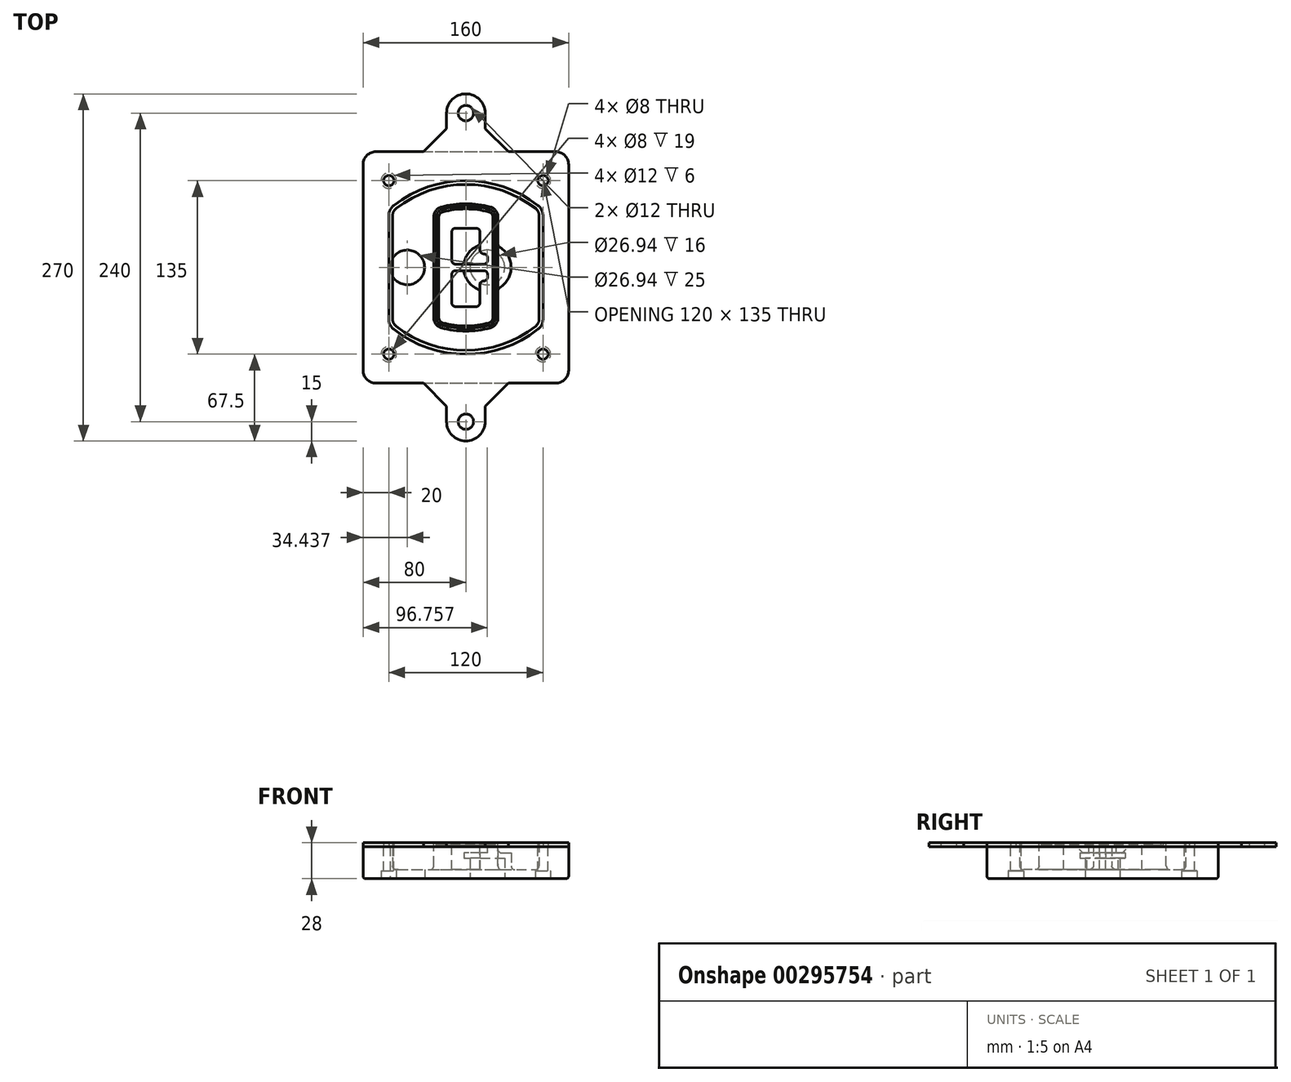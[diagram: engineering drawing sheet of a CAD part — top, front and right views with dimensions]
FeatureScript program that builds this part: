
annotation { "Feature Type Name" : "Feature", "Feature Type Description" : "" }
export const myFeature = defineFeature(function(context is Context, id is Id, definition is map)
    precondition{}
    {
        {
            var Q0;
            Q0=qCreatedBy(makeId("Top.planeOp"),FACE);
            var sketch = newSketch(context, id + "F0", { "sketchPlane" : qUnion([Q0])});
            skPoint(sketch, "E0.rect.middle", {"position": v(0, 0) * mm});
            skLineSegment(sketch, "E1.bottom", {"start": v(-70, -90) * mm, "end": v(70, -90) * mm});
            skLineSegment(sketch, "E1.top", {"start": v(-70, 90) * mm, "end": v(70, 90) * mm});
            skLineSegment(sketch, "E1.left", {"start": v(-80, -80) * mm, "end": v(-80, 80) * mm});
            skLineSegment(sketch, "E1.right", {"start": v(80, -80) * mm, "end": v(80, 80) * mm});
            skLineSegment(sketch, "E2", {"start": v(-80, 90) * mm, "end": v(80, -90) * mm, "construction": true});
            skLineSegment(sketch, "E3", {"start": v(80, 90) * mm, "end": v(-80, -90) * mm, "construction": true});
            skCircle(sketch, "E4", {"center": v(-60, 67.5) * mm, "radius": 4 * mm});
            skCircle(sketch, "E5", {"center": v(60, 67.5) * mm, "radius": 4 * mm});
            skCircle(sketch, "E6", {"center": v(60, -67.5) * mm, "radius": 4 * mm});
            skCircle(sketch, "E7", {"center": v(-60, -67.5) * mm, "radius": 4 * mm});
            skLineSegment(sketch, "E8", {"start": v(-60, 67.5) * mm, "end": v(60, 67.5) * mm, "construction": true});
            skLineSegment(sketch, "E9", {"start": v(60, 67.5) * mm, "end": v(60, -67.5) * mm, "construction": true});
            skLineSegment(sketch, "E10", {"start": v(60, -67.5) * mm, "end": v(-60, -67.5) * mm, "construction": true});
            skLineSegment(sketch, "E11", {"start": v(-60, -67.5) * mm, "end": v(-60, 67.5) * mm, "construction": true});
            skLineSegment(sketch, "E12", {"start": v(-60, 40.3) * mm, "end": v(-60, -40.3) * mm});
            skLineSegment(sketch, "E13", {"start": v(60, 40.3) * mm, "end": v(60, -40.3) * mm});
            skArc(sketch, "E14", {"start": v(56.15, 48.18) * mm, "mid": v(0, 67.5) * mm, "end": v(-56.15, 48.18) * mm});
            skArc(sketch, "E15", {"start": v(-56.15, -48.18) * mm, "mid": v(0, -67.5) * mm, "end": v(56.15, -48.18) * mm});
            skLineSegment(sketch, "E16", {"start": v(-60, 0) * mm, "end": v(60, 0) * mm, "construction": true});
            skPoint(sketch, "E17.visualSharp", {"position": v(-60, -45) * mm});
            skArc(sketch, "E17.filletArc", {"start": v(-60, -40.3) * mm, "mid": v(-58.99, -44.68) * mm, "end": v(-56.15, -48.18) * mm});
            skPoint(sketch, "E18.visualSharp", {"position": v(-60, 45) * mm});
            skArc(sketch, "E18.filletArc", {"start": v(-56.15, 48.18) * mm, "mid": v(-58.99, 44.68) * mm, "end": v(-60, 40.3) * mm});
            skPoint(sketch, "E19.visualSharp", {"position": v(60, 45) * mm});
            skArc(sketch, "E19.filletArc", {"start": v(60, 40.3) * mm, "mid": v(58.99, 44.68) * mm, "end": v(56.15, 48.18) * mm});
            skPoint(sketch, "E20.visualSharp", {"position": v(60, -45) * mm});
            skArc(sketch, "E20.filletArc", {"start": v(56.15, -48.18) * mm, "mid": v(58.99, -44.68) * mm, "end": v(60, -40.3) * mm});
            skPoint(sketch, "E21.visualSharp", {"position": v(-80, 90) * mm});
            skArc(sketch, "E21.filletArc", {"start": v(-70, 90) * mm, "mid": v(-77.07, 87.07) * mm, "end": v(-80, 80) * mm});
            skPoint(sketch, "E22.visualSharp", {"position": v(80, 90) * mm});
            skArc(sketch, "E22.filletArc", {"start": v(80, 80) * mm, "mid": v(77.07, 87.07) * mm, "end": v(70, 90) * mm});
            skPoint(sketch, "E23.visualSharp", {"position": v(80, -90) * mm});
            skArc(sketch, "E23.filletArc", {"start": v(70, -90) * mm, "mid": v(77.07, -87.07) * mm, "end": v(80, -80) * mm});
            skPoint(sketch, "E24.visualSharp", {"position": v(-80, -90) * mm});
            skArc(sketch, "E24.filletArc", {"start": v(-80, -80) * mm, "mid": v(-77.07, -87.07) * mm, "end": v(-70, -90) * mm});
            skArc(sketch, "E25.0", {"start": v(57, 40.3) * mm, "mid": v(56.3, 43.36) * mm, "end": v(54.3, 45.81) * mm});
            skLineSegment(sketch, "E25.1", {"start": v(57, 40.3) * mm, "end": v(57, -40.3) * mm});
            skArc(sketch, "E25.2", {"start": v(54.3, -45.81) * mm, "mid": v(56.3, -43.36) * mm, "end": v(57, -40.3) * mm});
            skArc(sketch, "E25.3", {"start": v(-54.3, -45.81) * mm, "mid": v(0, -64.5) * mm, "end": v(54.3, -45.81) * mm});
            skArc(sketch, "E25.4", {"start": v(-57, -40.3) * mm, "mid": v(-56.3, -43.36) * mm, "end": v(-54.3, -45.81) * mm});
            skArc(sketch, "E25.5", {"start": v(54.3, 45.81) * mm, "mid": v(0, 64.5) * mm, "end": v(-54.3, 45.81) * mm});
            skLineSegment(sketch, "E25.6", {"start": v(-57, 40.3) * mm, "end": v(-57, -40.3) * mm});
            skArc(sketch, "E25.7", {"start": v(-54.3, 45.81) * mm, "mid": v(-56.3, 43.36) * mm, "end": v(-57, 40.3) * mm});
            skArc(sketch, "E26.0", {"start": v(-58.62, 51.33) * mm, "mid": v(-62.58, 46.43) * mm, "end": v(-64, 40.3) * mm});
            skArc(sketch, "E26.1", {"start": v(58.62, 51.33) * mm, "mid": v(0, 71.5) * mm, "end": v(-58.62, 51.33) * mm});
            skArc(sketch, "E26.2", {"start": v(64, 40.3) * mm, "mid": v(62.58, 46.43) * mm, "end": v(58.62, 51.33) * mm});
            skLineSegment(sketch, "E26.3", {"start": v(64, 40.3) * mm, "end": v(64, -40.3) * mm});
            skArc(sketch, "E26.4", {"start": v(58.62, -51.33) * mm, "mid": v(62.58, -46.43) * mm, "end": v(64, -40.3) * mm});
            skLineSegment(sketch, "E26.5", {"start": v(-64, 40.3) * mm, "end": v(-64, -40.3) * mm});
            skArc(sketch, "E26.6", {"start": v(-58.62, -51.33) * mm, "mid": v(0, -71.5) * mm, "end": v(58.62, -51.33) * mm});
            skArc(sketch, "E26.7", {"start": v(-64, -40.3) * mm, "mid": v(-62.58, -46.43) * mm, "end": v(-58.62, -51.33) * mm});
            skSolve(sketch);
        }
        {
            var Q0;
            Q0=makeQuery(id+"F0.imprint","IMPRINT",FACE,{"disambiguationData":[TD([[makeQuery(id+"F0.imprint","IMPRINT",EDGE,{"derivedFrom":sQuery(id+"F0.wireOp",EDGE,"E1.bottom")}),1.0]])]});
            var Q1;
            Q1=makeQuery(id+"F0.imprint","IMPRINT",FACE,{"disambiguationData":[TD([[makeQuery(id+"F0.imprint","IMPRINT",EDGE,{"derivedFrom":sQuery(id+"F0.wireOp",EDGE,"E12")}),1.0]])]});
            var Q2;
            Q2=makeQuery(id+"F0.imprint","IMPRINT",FACE,{"disambiguationData":[TD([[makeQuery(id+"F0.imprint","IMPRINT",EDGE,{"derivedFrom":sQuery(id+"F0.wireOp",EDGE,"E25.0")}),1.0]])]});
            var Q3;
            Q3=makeQuery(id+"F0.imprint","IMPRINT",FACE,{"disambiguationData":[TD([[makeQuery(id+"F0.imprint","IMPRINT",EDGE,{"derivedFrom":sQuery(id+"F0.wireOp",EDGE,"E12")}),-1.0]])]});
            extrude(context, id + "F1", {"entities" : qUnion([Q0, Q1, Q2, Q3]), "oppositeDirection" : true, "depth" : 25 * mm});
        }
        {
            var Q0;
            Q0=makeQuery(id+"F0.imprint","IMPRINT",FACE,{"disambiguationData":[TD([[makeQuery(id+"F0.imprint","IMPRINT",EDGE,{"derivedFrom":sQuery(id+"F0.wireOp",EDGE,"E12")}),1.0]])]});
            extrude(context, id + "F2", {"entities" : qUnion([Q0]), "operationType" : NewBodyOperationType.ADD, "depth" : 3 * mm});
        }
        {
            var Q0;
            Q0=makeQuery(id+"F0.imprint","IMPRINT",FACE,{"disambiguationData":[TD([[makeQuery(id+"F0.imprint","IMPRINT",EDGE,{"derivedFrom":sQuery(id+"F0.wireOp",EDGE,"E25.0")}),1.0]])]});
            extrude(context, id + "F3", {"entities" : qUnion([Q0]), "operationType" : NewBodyOperationType.REMOVE, "oppositeDirection" : true, "depth" : 18 * mm});
        }
        {
            var Q0;
            Q0=makeQuery(id+"F2.opExtrude","CAP_FACE",FACE,{"disambiguationData":[OSD([sQuery(id+"F0.wireOp",EDGE,"E12"),sQuery(id+"F0.wireOp",EDGE,"E13"),sQuery(id+"F0.wireOp",EDGE,"E14"),sQuery(id+"F0.wireOp",EDGE,"E15"),sQuery(id+"F0.wireOp",EDGE,"E17.filletArc"),sQuery(id+"F0.wireOp",EDGE,"E18.filletArc"),sQuery(id+"F0.wireOp",EDGE,"E19.filletArc"),sQuery(id+"F0.wireOp",EDGE,"E20.filletArc"),sQuery(id+"F0.wireOp",EDGE,"E25.0"),sQuery(id+"F0.wireOp",EDGE,"E25.1"),sQuery(id+"F0.wireOp",EDGE,"E25.2"),sQuery(id+"F0.wireOp",EDGE,"E25.3"),sQuery(id+"F0.wireOp",EDGE,"E25.4"),sQuery(id+"F0.wireOp",EDGE,"E25.5"),sQuery(id+"F0.wireOp",EDGE,"E25.6"),sQuery(id+"F0.wireOp",EDGE,"E25.7")])],"isStart":false});
            var sketch = newSketch(context, id + "F4", { "sketchPlane" : qUnion([Q0])});
            skArc(sketch, "E27.0", {"start": v(-19.08, -46.97) * mm, "mid": v(0, -49.5) * mm, "end": v(19.08, -46.97) * mm});
            skArc(sketch, "E28.0", {"start": v(19.08, 46.97) * mm, "mid": v(0, 49.5) * mm, "end": v(-19.08, 46.97) * mm});
            skLineSegment(sketch, "E29", {"start": v(-25, 39.25) * mm, "end": v(-25, -39.25) * mm});
            skLineSegment(sketch, "E30", {"start": v(25, 39.25) * mm, "end": v(25, -39.25) * mm});
            skLineSegment(sketch, "E31", {"start": v(-25, 45.1) * mm, "end": v(25, 45.1) * mm, "construction": true});
            skLineSegment(sketch, "E32", {"start": v(-25, -45.1) * mm, "end": v(25, -45.1) * mm, "construction": true});
            skPoint(sketch, "E33.visualSharp", {"position": v(-25, 45.1) * mm});
            skArc(sketch, "E33.filletArc", {"start": v(-19.08, 46.97) * mm, "mid": v(-23.35, 44.11) * mm, "end": v(-25, 39.25) * mm});
            skPoint(sketch, "E34.visualSharp", {"position": v(25, 45.1) * mm});
            skArc(sketch, "E34.filletArc", {"start": v(25, 39.25) * mm, "mid": v(23.35, 44.11) * mm, "end": v(19.08, 46.97) * mm});
            skPoint(sketch, "E35.visualSharp", {"position": v(25, -45.1) * mm});
            skArc(sketch, "E35.filletArc", {"start": v(19.08, -46.97) * mm, "mid": v(23.35, -44.11) * mm, "end": v(25, -39.25) * mm});
            skPoint(sketch, "E36.visualSharp", {"position": v(-25, -45.1) * mm});
            skArc(sketch, "E36.filletArc", {"start": v(-25, -39.25) * mm, "mid": v(-23.35, -44.11) * mm, "end": v(-19.08, -46.97) * mm});
            skArc(sketch, "E37.0", {"start": v(54.3, 45.81) * mm, "mid": v(0, 64.5) * mm, "end": v(-54.3, 45.81) * mm});
            skArc(sketch, "E37.1", {"start": v(-54.3, 45.81) * mm, "mid": v(-56.3, 43.36) * mm, "end": v(-57, 40.3) * mm});
            skLineSegment(sketch, "E37.2", {"start": v(-57, 40.3) * mm, "end": v(-57, -40.3) * mm});
            skArc(sketch, "E37.3", {"start": v(-57, -40.3) * mm, "mid": v(-56.3, -43.36) * mm, "end": v(-54.3, -45.81) * mm});
            skArc(sketch, "E37.4", {"start": v(-54.3, -45.81) * mm, "mid": v(0, -64.5) * mm, "end": v(54.3, -45.81) * mm});
            skArc(sketch, "E37.5", {"start": v(54.3, -45.81) * mm, "mid": v(56.3, -43.36) * mm, "end": v(57, -40.3) * mm});
            skLineSegment(sketch, "E37.6", {"start": v(57, 40.3) * mm, "end": v(57, -40.3) * mm});
            skArc(sketch, "E37.7", {"start": v(57, 40.3) * mm, "mid": v(56.3, 43.36) * mm, "end": v(54.3, 45.81) * mm});
            skLineSegment(sketch, "E38.0", {"start": v(23, 39.25) * mm, "end": v(23, -39.25) * mm});
            skArc(sketch, "E38.1", {"start": v(18.56, -45.04) * mm, "mid": v(21.76, -42.9) * mm, "end": v(23, -39.25) * mm});
            skArc(sketch, "E38.2", {"start": v(-18.56, -45.04) * mm, "mid": v(0, -47.5) * mm, "end": v(18.56, -45.04) * mm});
            skArc(sketch, "E38.3", {"start": v(-23, -39.25) * mm, "mid": v(-21.76, -42.9) * mm, "end": v(-18.56, -45.04) * mm});
            skLineSegment(sketch, "E38.4", {"start": v(-23, 39.25) * mm, "end": v(-23, -39.25) * mm});
            skArc(sketch, "E38.5", {"start": v(23, 39.25) * mm, "mid": v(21.76, 42.9) * mm, "end": v(18.56, 45.04) * mm});
            skArc(sketch, "E38.6", {"start": v(-18.56, 45.04) * mm, "mid": v(-21.76, 42.9) * mm, "end": v(-23, 39.25) * mm});
            skArc(sketch, "E38.7", {"start": v(18.56, 45.04) * mm, "mid": v(0, 47.5) * mm, "end": v(-18.56, 45.04) * mm});
            skArc(sketch, "E39.0", {"start": v(21, 39.25) * mm, "mid": v(20.18, 41.68) * mm, "end": v(18.04, 43.1) * mm});
            skLineSegment(sketch, "E39.1", {"start": v(21, 39.25) * mm, "end": v(21, -39.25) * mm});
            skArc(sketch, "E39.2", {"start": v(18.04, -43.1) * mm, "mid": v(20.18, -41.68) * mm, "end": v(21, -39.25) * mm});
            skArc(sketch, "E39.3", {"start": v(-18.04, -43.1) * mm, "mid": v(0, -45.5) * mm, "end": v(18.04, -43.1) * mm});
            skArc(sketch, "E39.4", {"start": v(-21, -39.25) * mm, "mid": v(-20.18, -41.68) * mm, "end": v(-18.04, -43.1) * mm});
            skArc(sketch, "E39.5", {"start": v(18.04, 43.1) * mm, "mid": v(0, 45.5) * mm, "end": v(-18.04, 43.1) * mm});
            skLineSegment(sketch, "E39.6", {"start": v(-21, 39.25) * mm, "end": v(-21, -39.25) * mm});
            skArc(sketch, "E39.7", {"start": v(-18.04, 43.1) * mm, "mid": v(-20.18, 41.68) * mm, "end": v(-21, 39.25) * mm});
            skLineSegment(sketch, "E40", {"start": v(-25, 0) * mm, "end": v(25, 0) * mm, "construction": true});
            skLineSegment(sketch, "E41", {"start": v(-11, 5.5) * mm, "end": v(-11, 27.5) * mm});
            skLineSegment(sketch, "E42", {"start": v(-8, 30.5) * mm, "end": v(8, 30.5) * mm});
            skLineSegment(sketch, "E43", {"start": v(11, 27.5) * mm, "end": v(11, 13.5) * mm});
            skLineSegment(sketch, "E44", {"start": v(14, 10.5) * mm, "end": v(14, 10.5) * mm});
            skLineSegment(sketch, "E45", {"start": v(17, 7.5) * mm, "end": v(17, 5.5) * mm});
            skLineSegment(sketch, "E46", {"start": v(14, 2.5) * mm, "end": v(-8, 2.5) * mm});
            skPoint(sketch, "E47.visualSharp", {"position": v(-11, 30.5) * mm});
            skArc(sketch, "E47.filletArc", {"start": v(-8, 30.5) * mm, "mid": v(-10.12, 29.62) * mm, "end": v(-11, 27.5) * mm});
            skPoint(sketch, "E48.visualSharp", {"position": v(11, 30.5) * mm});
            skArc(sketch, "E48.filletArc", {"start": v(11, 27.5) * mm, "mid": v(10.12, 29.62) * mm, "end": v(8, 30.5) * mm});
            skPoint(sketch, "E49.visualSharp", {"position": v(11, 10.5) * mm});
            skArc(sketch, "E49.filletArc", {"start": v(11, 13.5) * mm, "mid": v(11.88, 11.38) * mm, "end": v(14, 10.5) * mm});
            skPoint(sketch, "E50.visualSharp", {"position": v(17, 10.5) * mm});
            skArc(sketch, "E50.filletArc", {"start": v(17, 7.5) * mm, "mid": v(16.12, 9.62) * mm, "end": v(14, 10.5) * mm});
            skPoint(sketch, "E51.visualSharp", {"position": v(17, 2.5) * mm});
            skArc(sketch, "E51.filletArc", {"start": v(14, 2.5) * mm, "mid": v(16.12, 3.38) * mm, "end": v(17, 5.5) * mm});
            skPoint(sketch, "E52.visualSharp", {"position": v(-11, 2.5) * mm});
            skArc(sketch, "E52.filletArc", {"start": v(-11, 5.5) * mm, "mid": v(-10.12, 3.38) * mm, "end": v(-8, 2.5) * mm});
            skLineSegment(sketch, "E53.0.MirrorCS", {"start": v(14, -2.5) * mm, "end": v(-8, -2.5) * mm});
            skArc(sketch, "E54.0.MirrorCS", {"start": v(-11, -5.5) * mm, "mid": v(-10.12, -3.38) * mm, "end": v(-8, -2.5) * mm});
            skLineSegment(sketch, "E55.0.MirrorCS", {"start": v(-11, -5.5) * mm, "end": v(-11, -27.5) * mm});
            skArc(sketch, "E56.0.MirrorCS", {"start": v(-8, -30.5) * mm, "mid": v(-10.12, -29.62) * mm, "end": v(-11, -27.5) * mm});
            skLineSegment(sketch, "E57.0.MirrorCS", {"start": v(-8, -30.5) * mm, "end": v(8, -30.5) * mm});
            skArc(sketch, "E58.0.MirrorCS", {"start": v(11, -27.5) * mm, "mid": v(10.12, -29.62) * mm, "end": v(8, -30.5) * mm});
            skLineSegment(sketch, "E59.0.MirrorCS", {"start": v(11, -27.5) * mm, "end": v(11, -13.5) * mm});
            skArc(sketch, "E60.0.MirrorCS", {"start": v(11, -13.5) * mm, "mid": v(11.88, -11.38) * mm, "end": v(14, -10.5) * mm});
            skArc(sketch, "E61.0.MirrorCS", {"start": v(17, -7.5) * mm, "mid": v(16.12, -9.62) * mm, "end": v(14, -10.5) * mm});
            skLineSegment(sketch, "E62.0.MirrorCS", {"start": v(17, -7.5) * mm, "end": v(17, -5.5) * mm});
            skArc(sketch, "E63.0.MirrorCS", {"start": v(14, -2.5) * mm, "mid": v(16.12, -3.38) * mm, "end": v(17, -5.5) * mm});
            skSolve(sketch);
        }
        {
            var Q0;
            Q0=makeQuery(id+"F4.imprint","IMPRINT",FACE,{"disambiguationData":[TD([[makeQuery(id+"F4.imprint","IMPRINT",EDGE,{"derivedFrom":sQuery(id+"F4.wireOp",EDGE,"E27.0")}),1.0]])]});
            var Q1;
            Q1=makeQuery(id+"F4.imprint","IMPRINT",FACE,{"disambiguationData":[TD([[makeQuery(id+"F4.imprint","IMPRINT",EDGE,{"derivedFrom":sQuery(id+"F4.wireOp",EDGE,"E38.0")}),-1.0]])]});
            var Q2;
            Q2=makeQuery(id+"F4.imprint","IMPRINT",FACE,{"disambiguationData":[TD([[makeQuery(id+"F4.imprint","IMPRINT",EDGE,{"derivedFrom":sQuery(id+"F4.wireOp",EDGE,"E39.0")}),1.0]])]});
            extrude(context, id + "F5", {"entities" : qUnion([Q0, Q1, Q2]), "operationType" : NewBodyOperationType.ADD, "endBound" : BoundingType.UP_TO_NEXT, "oppositeDirection" : true, "depth" : 25 * mm});
        }
        {
            var Q0;
            Q0=makeQuery(id+"F4.imprint","IMPRINT",FACE,{"disambiguationData":[TD([[makeQuery(id+"F4.imprint","IMPRINT",EDGE,{"derivedFrom":sQuery(id+"F4.wireOp",EDGE,"E38.0")}),-1.0]])]});
            extrude(context, id + "F6", {"entities" : qUnion([Q0]), "operationType" : NewBodyOperationType.REMOVE, "oppositeDirection" : true, "depth" : 2 * mm});
        }
        {
            var Q0;
            Q0=makeQuery(id+"F1.opExtrude","CAP_FACE",FACE,{"disambiguationData":[OSD([sQuery(id+"F0.wireOp",EDGE,"E1.bottom"),sQuery(id+"F0.wireOp",EDGE,"E1.top"),sQuery(id+"F0.wireOp",EDGE,"E1.left"),sQuery(id+"F0.wireOp",EDGE,"E1.right"),sQuery(id+"F0.wireOp",EDGE,"E4"),sQuery(id+"F0.wireOp",EDGE,"E5"),sQuery(id+"F0.wireOp",EDGE,"E6"),sQuery(id+"F0.wireOp",EDGE,"E7"),sQuery(id+"F0.wireOp",EDGE,"E21.filletArc"),sQuery(id+"F0.wireOp",EDGE,"E22.filletArc"),sQuery(id+"F0.wireOp",EDGE,"E23.filletArc"),sQuery(id+"F0.wireOp",EDGE,"E24.filletArc")])],"isStart":false});
            var sketch = newSketch(context, id + "F7", { "sketchPlane" : qUnion([Q0])});
            skCircle(sketch, "E64", {"center": v(16.76, 0) * mm, "radius": 13.47 * mm});
            skCircle(sketch, "E65", {"center": v(-45.56, 0) * mm, "radius": 13.47 * mm});
            skLineSegment(sketch, "E66", {"start": v(80, 0) * mm, "end": v(-80, 0) * mm});
            skCircle(sketch, "E67", {"center": v(16.76, 0) * mm, "radius": 18.47 * mm});
            skCircle(sketch, "E68", {"center": v(60, -67.5) * mm, "radius": 6 * mm});
            skCircle(sketch, "E69", {"center": v(-60, -67.5) * mm, "radius": 6 * mm});
            skCircle(sketch, "E70", {"center": v(-60, 67.5) * mm, "radius": 6 * mm});
            skCircle(sketch, "E71", {"center": v(60, 67.5) * mm, "radius": 6 * mm});
            skSolve(sketch);
        }
        {
            var Q0;
            {var subQ1=sQuery(id+"F7.wireOp",EDGE,"E66");var subQ4=sQuery(id+"F7.wireOp",EDGE,"E64");var subQ6=makeQuery(id+"F7.imprint","INTERSECT",VERTEX,{"disambiguationData":[OD(0.0)],"derivedFrom":[subQ4,subQ1]});Q0=makeQuery(id+"F7.imprint","IMPRINT",FACE,{"disambiguationData":[TD([[makeQuery(id+"F7.imprint","IMPRINT",EDGE,{"disambiguationData":[TD([[subQ6,-1.0]])],"derivedFrom":subQ4}),-1.0]])]});}
            var Q1;
            {var subQ0=sQuery(id+"F7.wireOp",EDGE,"E66");var subQ1=sQuery(id+"F7.wireOp",EDGE,"E64");var subQ3=makeQuery(id+"F7.imprint","INTERSECT",VERTEX,{"disambiguationData":[OD(0.0)],"derivedFrom":[subQ1,subQ0]});Q1=makeQuery(id+"F7.imprint","IMPRINT",FACE,{"disambiguationData":[TD([[makeQuery(id+"F7.imprint","IMPRINT",EDGE,{"disambiguationData":[TD([[subQ3,-1.0]])],"derivedFrom":subQ1}),1.0]])]});}
            var Q2;
            {var subQ0=sQuery(id+"F7.wireOp",EDGE,"E66");var subQ1=sQuery(id+"F7.wireOp",EDGE,"E64");var subQ3=makeQuery(id+"F7.imprint","INTERSECT",VERTEX,{"disambiguationData":[OD(0.0)],"derivedFrom":[subQ1,subQ0]});Q2=makeQuery(id+"F7.imprint","IMPRINT",FACE,{"disambiguationData":[TD([[makeQuery(id+"F7.imprint","IMPRINT",EDGE,{"disambiguationData":[TD([[subQ3,1.0]])],"derivedFrom":subQ1}),1.0]])]});}
            var Q3;
            {var subQ1=sQuery(id+"F7.wireOp",EDGE,"E66");var subQ4=sQuery(id+"F7.wireOp",EDGE,"E64");var subQ6=makeQuery(id+"F7.imprint","INTERSECT",VERTEX,{"disambiguationData":[OD(0.0)],"derivedFrom":[subQ4,subQ1]});Q3=makeQuery(id+"F7.imprint","IMPRINT",FACE,{"disambiguationData":[TD([[makeQuery(id+"F7.imprint","IMPRINT",EDGE,{"disambiguationData":[TD([[subQ6,1.0]])],"derivedFrom":subQ4}),-1.0]])]});}
            extrude(context, id + "F8", {"entities" : qUnion([Q0, Q1, Q2, Q3]), "operationType" : NewBodyOperationType.ADD, "oppositeDirection" : true, "depth" : 20 * mm});
        }
        {
            var Q0;
            {var subQ0=sQuery(id+"F7.wireOp",EDGE,"E66");var subQ1=sQuery(id+"F7.wireOp",EDGE,"E64");var subQ3=makeQuery(id+"F7.imprint","INTERSECT",VERTEX,{"disambiguationData":[OD(0.0)],"derivedFrom":[subQ1,subQ0]});Q0=makeQuery(id+"F7.imprint","IMPRINT",FACE,{"disambiguationData":[TD([[makeQuery(id+"F7.imprint","IMPRINT",EDGE,{"disambiguationData":[TD([[subQ3,-1.0]])],"derivedFrom":subQ1}),1.0]])]});}
            var Q1;
            {var subQ0=sQuery(id+"F7.wireOp",EDGE,"E66");var subQ1=sQuery(id+"F7.wireOp",EDGE,"E64");var subQ3=makeQuery(id+"F7.imprint","INTERSECT",VERTEX,{"disambiguationData":[OD(0.0)],"derivedFrom":[subQ1,subQ0]});Q1=makeQuery(id+"F7.imprint","IMPRINT",FACE,{"disambiguationData":[TD([[makeQuery(id+"F7.imprint","IMPRINT",EDGE,{"disambiguationData":[TD([[subQ3,1.0]])],"derivedFrom":subQ1}),1.0]])]});}
            extrude(context, id + "F9", {"entities" : qUnion([Q0, Q1]), "operationType" : NewBodyOperationType.REMOVE, "oppositeDirection" : true, "depth" : 16 * mm});
        }
        {
            var Q0;
            {var subQ0=sQuery(id+"F7.wireOp",EDGE,"E66");var subQ1=sQuery(id+"F7.wireOp",EDGE,"E65");var subQ3=makeQuery(id+"F7.imprint","INTERSECT",VERTEX,{"disambiguationData":[OD(0.0)],"derivedFrom":[subQ1,subQ0]});Q0=makeQuery(id+"F7.imprint","IMPRINT",FACE,{"disambiguationData":[TD([[makeQuery(id+"F7.imprint","IMPRINT",EDGE,{"disambiguationData":[TD([[subQ3,-1.0]])],"derivedFrom":subQ1}),1.0]])]});}
            var Q1;
            {var subQ0=sQuery(id+"F7.wireOp",EDGE,"E66");var subQ1=sQuery(id+"F7.wireOp",EDGE,"E65");var subQ3=makeQuery(id+"F7.imprint","INTERSECT",VERTEX,{"disambiguationData":[OD(0.0)],"derivedFrom":[subQ1,subQ0]});Q1=makeQuery(id+"F7.imprint","IMPRINT",FACE,{"disambiguationData":[TD([[makeQuery(id+"F7.imprint","IMPRINT",EDGE,{"disambiguationData":[TD([[subQ3,1.0]])],"derivedFrom":subQ1}),1.0]])]});}
            extrude(context, id + "F10", {"entities" : qUnion([Q0, Q1]), "operationType" : NewBodyOperationType.REMOVE, "oppositeDirection" : true, "depth" : 25 * mm});
        }
        {
            var Q0;
            Q0=makeQuery(id+"F7.imprint","IMPRINT",FACE,{"disambiguationData":[TD([[makeQuery(id+"F7.imprint","IMPRINT",EDGE,{"derivedFrom":sQuery(id+"F7.wireOp",EDGE,"E68")}),1.0]])]});
            var Q1;
            Q1=makeQuery(id+"F7.imprint","IMPRINT",FACE,{"disambiguationData":[TD([[makeQuery(id+"F7.imprint","IMPRINT",EDGE,{"derivedFrom":makeQuery(id+"F1.opExtrude","CAP_EDGE",EDGE,{"disambiguationData":[OSD([sQuery(id+"F0.wireOp",EDGE,"E5")])],"isStart":false})}),-1.0]])]});
            var Q2;
            Q2=makeQuery(id+"F7.imprint","IMPRINT",FACE,{"disambiguationData":[TD([[makeQuery(id+"F7.imprint","IMPRINT",EDGE,{"derivedFrom":sQuery(id+"F7.wireOp",EDGE,"E69")}),1.0]])]});
            var Q3;
            Q3=makeQuery(id+"F7.imprint","IMPRINT",FACE,{"disambiguationData":[TD([[makeQuery(id+"F7.imprint","IMPRINT",EDGE,{"derivedFrom":makeQuery(id+"F1.opExtrude","CAP_EDGE",EDGE,{"disambiguationData":[OSD([sQuery(id+"F0.wireOp",EDGE,"E4")])],"isStart":false})}),-1.0]])]});
            var Q4;
            Q4=makeQuery(id+"F7.imprint","IMPRINT",FACE,{"disambiguationData":[TD([[makeQuery(id+"F7.imprint","IMPRINT",EDGE,{"derivedFrom":sQuery(id+"F7.wireOp",EDGE,"E70")}),1.0]])]});
            var Q5;
            Q5=makeQuery(id+"F7.imprint","IMPRINT",FACE,{"disambiguationData":[TD([[makeQuery(id+"F7.imprint","IMPRINT",EDGE,{"derivedFrom":makeQuery(id+"F1.opExtrude","CAP_EDGE",EDGE,{"disambiguationData":[OSD([sQuery(id+"F0.wireOp",EDGE,"E7")])],"isStart":false})}),-1.0]])]});
            var Q6;
            Q6=makeQuery(id+"F7.imprint","IMPRINT",FACE,{"disambiguationData":[TD([[makeQuery(id+"F7.imprint","IMPRINT",EDGE,{"derivedFrom":sQuery(id+"F7.wireOp",EDGE,"E71")}),1.0]])]});
            var Q7;
            Q7=makeQuery(id+"F7.imprint","IMPRINT",FACE,{"disambiguationData":[TD([[makeQuery(id+"F7.imprint","IMPRINT",EDGE,{"derivedFrom":makeQuery(id+"F1.opExtrude","CAP_EDGE",EDGE,{"disambiguationData":[OSD([sQuery(id+"F0.wireOp",EDGE,"E6")])],"isStart":false})}),-1.0]])]});
            extrude(context, id + "F11", {"entities" : qUnion([Q0, Q1, Q2, Q3, Q4, Q5, Q6, Q7]), "operationType" : NewBodyOperationType.REMOVE, "oppositeDirection" : true, "depth" : 6 * mm});
        }
        {
            var Q0;
            Q0=makeQuery(id+"F9.boolean.opBoolean","COPY",FACE,{"derivedFrom":makeQuery(id+"F9.opExtrude","CAP_FACE",FACE,{"disambiguationData":[OSD([sQuery(id+"F7.wireOp",EDGE,"E64")])],"isStart":false})});
            var sketch = newSketch(context, id + "F12", { "sketchPlane" : qUnion([Q0])});
            skArc(sketch, "E72.0", {"start": v(11, 17.55) * mm, "mid": v(2.57, 11.82) * mm, "end": v(-1.54, 2.5) * mm});
            skArc(sketch, "E72.1", {"start": v(-1.54, -2.5) * mm, "mid": v(2.57, -11.82) * mm, "end": v(11, -17.55) * mm});
            skLineSegment(sketch, "E73", {"start": v(-1.54, -2.5) * mm, "end": v(14, -2.5) * mm});
            skLineSegment(sketch, "E74.0", {"start": v(14, 2.5) * mm, "end": v(-1.54, 2.5) * mm});
            skArc(sketch, "E74.1", {"start": v(14, 2.5) * mm, "mid": v(16.12, 3.38) * mm, "end": v(17, 5.5) * mm});
            skLineSegment(sketch, "E74.2", {"start": v(17, 7.5) * mm, "end": v(17, 5.5) * mm});
            skArc(sketch, "E74.3", {"start": v(17, 7.5) * mm, "mid": v(16.12, 9.62) * mm, "end": v(14, 10.5) * mm});
            skArc(sketch, "E74.4", {"start": v(11, 13.5) * mm, "mid": v(11.88, 11.38) * mm, "end": v(14, 10.5) * mm});
            skLineSegment(sketch, "E74.5", {"start": v(11, 17.55) * mm, "end": v(11, 13.5) * mm});
            skLineSegment(sketch, "E74.7", {"start": v(14, -2.5) * mm, "end": v(-1.54, -2.5) * mm});
            skArc(sketch, "E74.8", {"start": v(14, -2.5) * mm, "mid": v(16.12, -3.38) * mm, "end": v(17, -5.5) * mm});
            skLineSegment(sketch, "E74.9", {"start": v(17, -7.5) * mm, "end": v(17, -5.5) * mm});
            skArc(sketch, "E74.10", {"start": v(17, -7.5) * mm, "mid": v(16.12, -9.62) * mm, "end": v(14, -10.5) * mm});
            skArc(sketch, "E74.11", {"start": v(11, -13.5) * mm, "mid": v(11.88, -11.38) * mm, "end": v(14, -10.5) * mm});
            skLineSegment(sketch, "E74.12", {"start": v(11, -17.55) * mm, "end": v(11, -13.5) * mm});
            skPoint(sketch, "E75.orphan", {"position": v(11, -27.5) * mm});
            skPoint(sketch, "E76.orphan", {"position": v(-8, -2.5) * mm});
            skPoint(sketch, "E77.orphan", {"position": v(-8, 2.5) * mm});
            skPoint(sketch, "E78.orphan", {"position": v(11, 27.5) * mm});
            skSolve(sketch);
        }
        {
            var Q0;
            {var subQ7=sQuery(id+"F12.wireOp",EDGE,"E72.0");var subQ14=sQuery(id+"F12.wireOp",EDGE,"E72.1");var subQ16=sQuery(id+"F12.wireOp",EDGE,"E74.1");var subQ18=sQuery(id+"F12.wireOp",EDGE,"E74.8");Q0=qUnion([makeQuery(id+"F12.imprint","IMPRINT",FACE,{"disambiguationData":[TD([[makeQuery(id+"F12.imprint","IMPRINT",EDGE,{"derivedFrom":subQ7}),1.0]])]}),makeQuery(id+"F12.imprint","IMPRINT",FACE,{"disambiguationData":[TD([[makeQuery(id+"F12.imprint","IMPRINT",EDGE,{"derivedFrom":subQ14}),1.0]])]}),makeQuery(id+"F12.imprint","IMPRINT",FACE,{"disambiguationData":[TD([[makeQuery(id+"F12.imprint","IMPRINT",EDGE,{"derivedFrom":subQ16}),1.0]])]}),makeQuery(id+"F12.imprint","IMPRINT",FACE,{"disambiguationData":[TD([[makeQuery(id+"F12.imprint","IMPRINT",EDGE,{"derivedFrom":subQ18}),-1.0]])]})]);}
            var Q1;
            Q1=makeQuery(id+"F5.boolean.opBoolean","SPLIT",FACE,{"disambiguationData":[TD([makeQuery(id+"F5.opExtrude","SWEPT_FACE",FACE,{"disambiguationData":[OSD([sQuery(id+"F4.wireOp",EDGE,"E41")])]})])],"derivedFrom":makeQuery(id+"F3.boolean.opBoolean","COPY",FACE,{"derivedFrom":makeQuery(id+"F3.opExtrude","CAP_FACE",FACE,{"disambiguationData":[OSD([sQuery(id+"F0.wireOp",EDGE,"E25.0"),sQuery(id+"F0.wireOp",EDGE,"E25.1"),sQuery(id+"F0.wireOp",EDGE,"E25.2"),sQuery(id+"F0.wireOp",EDGE,"E25.3"),sQuery(id+"F0.wireOp",EDGE,"E25.4"),sQuery(id+"F0.wireOp",EDGE,"E25.5"),sQuery(id+"F0.wireOp",EDGE,"E25.6"),sQuery(id+"F0.wireOp",EDGE,"E25.7")])],"isStart":false})})});
            extrude(context, id + "F13", {"entities" : qUnion([Q0]), "operationType" : NewBodyOperationType.REMOVE, "endBound" : BoundingType.UP_TO_SURFACE, "endBoundEntityFace" : qUnion([Q1]), "depth" : 25 * mm});
        }
        {
            var Q0;
            Q0=makeQuery(id+"F3.boolean.opBoolean","COPY",EDGE,{"derivedFrom":makeQuery(id+"F3.opExtrude","CAP_EDGE",EDGE,{"disambiguationData":[OSD([sQuery(id+"F0.wireOp",EDGE,"E25.6")])],"isStart":false})});
            var Q1;
            Q1=makeQuery(id+"F8.boolean.opBoolean","INTERSECT",EDGE,{"derivedFrom":[makeQuery(id+"F5.opExtrude","SWEPT_FACE",FACE,{"disambiguationData":[OSD([sQuery(id+"F4.wireOp",EDGE,"E30")])]}),makeQuery(id+"F8.opExtrude","CAP_FACE",FACE,{"disambiguationData":[OSD([sQuery(id+"F7.wireOp",EDGE,"E67")])],"isStart":false})]});
            var Q2;
            Q2=makeQuery(id+"F8.boolean.opBoolean","INTERSECT",EDGE,{"disambiguationData":[OD(1.0)],"derivedFrom":[makeQuery(id+"F5.opExtrude","SWEPT_FACE",FACE,{"disambiguationData":[OSD([sQuery(id+"F4.wireOp",EDGE,"E30")])]}),makeQuery(id+"F8.opExtrude","SWEPT_FACE",FACE,{"disambiguationData":[OSD([sQuery(id+"F7.wireOp",EDGE,"E67")])]})]});
            var Q3;
            {var subQ0=sQuery(id+"F4.wireOp",EDGE,"E30");Q3=makeQuery(id+"F8.boolean.opBoolean","SPLIT",EDGE,{"disambiguationData":[TD([makeQuery(id+"F5.opExtrude","SWEPT_FACE",FACE,{"disambiguationData":[OSD([sQuery(id+"F4.wireOp",EDGE,"E35.filletArc")])]})])],"derivedFrom":makeQuery(id+"F5.opExtrude","CAP_EDGE",EDGE,{"disambiguationData":[OSD([subQ0])],"isStart":false})});}
            var Q4;
            {var subQ0=sQuery(id+"F0.wireOp",EDGE,"E25.7");var subQ1=sQuery(id+"F0.wireOp",EDGE,"E25.1");var subQ2=sQuery(id+"F0.wireOp",EDGE,"E25.6");var subQ3=sQuery(id+"F0.wireOp",EDGE,"E25.5");var subQ4=sQuery(id+"F0.wireOp",EDGE,"E25.4");var subQ5=sQuery(id+"F0.wireOp",EDGE,"E25.0");var subQ6=sQuery(id+"F0.wireOp",EDGE,"E25.2");var subQ7=sQuery(id+"F0.wireOp",EDGE,"E25.3");Q4=makeQuery(id+"F8.boolean.opBoolean","INTERSECT",EDGE,{"derivedFrom":[makeQuery(id+"F5.boolean.opBoolean","SPLIT",FACE,{"disambiguationData":[TD([makeQuery(id+"F2.opExtrude","SWEPT_FACE",FACE,{"disambiguationData":[OSD([subQ5])]})])],"derivedFrom":makeQuery(id+"F3.boolean.opBoolean","COPY",FACE,{"derivedFrom":makeQuery(id+"F3.opExtrude","CAP_FACE",FACE,{"disambiguationData":[OSD([subQ5,subQ1,subQ6,subQ7,subQ4,subQ3,subQ2,subQ0])],"isStart":false})})}),makeQuery(id+"F8.opExtrude","SWEPT_FACE",FACE,{"disambiguationData":[OSD([sQuery(id+"F7.wireOp",EDGE,"E67")])]})]});}
            var Q5;
            Q5=makeQuery(id+"F8.boolean.opBoolean","INTERSECT",EDGE,{"disambiguationData":[OD(0.0)],"derivedFrom":[makeQuery(id+"F5.opExtrude","SWEPT_FACE",FACE,{"disambiguationData":[OSD([sQuery(id+"F4.wireOp",EDGE,"E30")])]}),makeQuery(id+"F8.opExtrude","SWEPT_FACE",FACE,{"disambiguationData":[OSD([sQuery(id+"F7.wireOp",EDGE,"E67")])]})]});
            fillet(context, id + "F14", {"entities" : qUnion([Q0, Q1, Q2, Q3, Q4, Q5]), "radius" : 3 * mm, "tangentPropagation" : true, "allowEdgeOverflow" : false});
        }
        {
            var Q0;
            Q0=makeQuery(id+"F1.opExtrude","CAP_EDGE",EDGE,{"disambiguationData":[OSD([sQuery(id+"F0.wireOp",EDGE,"E1.bottom")])],"isStart":false});
            fillet(context, id + "F15", {"entities" : qUnion([Q0]), "radius" : 2 * mm, "tangentPropagation" : true, "allowEdgeOverflow" : false});
        }
        {
            var Q0;
            {var subQ0=sQuery(id+"F0.wireOp",EDGE,"E21.filletArc");var subQ1=sQuery(id+"F0.wireOp",EDGE,"E7");var subQ2=sQuery(id+"F0.wireOp",EDGE,"E6");var subQ3=sQuery(id+"F0.wireOp",EDGE,"E5");var subQ4=sQuery(id+"F0.wireOp",EDGE,"E4");var subQ5=sQuery(id+"F0.wireOp",EDGE,"E22.filletArc");var subQ6=sQuery(id+"F0.wireOp",EDGE,"E1.bottom");var subQ7=sQuery(id+"F0.wireOp",EDGE,"E1.right");var subQ8=sQuery(id+"F0.wireOp",EDGE,"E1.top");var subQ9=sQuery(id+"F0.wireOp",EDGE,"E1.left");var subQ10=sQuery(id+"F0.wireOp",EDGE,"E23.filletArc");var subQ11=sQuery(id+"F0.wireOp",EDGE,"E24.filletArc");Q0=makeQuery(id+"F2.boolean.opBoolean","SPLIT",FACE,{"disambiguationData":[TD([makeQuery(id+"F1.opExtrude","SWEPT_FACE",FACE,{"disambiguationData":[OSD([subQ6])]})])],"derivedFrom":makeQuery(id+"F1.opExtrude","CAP_FACE",FACE,{"disambiguationData":[OSD([subQ6,subQ8,subQ9,subQ7,subQ4,subQ3,subQ2,subQ1,subQ0,subQ5,subQ10,subQ11])],"isStart":true})});}
            var sketch = newSketch(context, id + "F16", { "sketchPlane" : qUnion([Q0])});
            skLineSegment(sketch, "E79", {"start": v(0, 90) * mm, "end": v(0, 120) * mm, "construction": true});
            skLineSegment(sketch, "E80", {"start": v(-15, 120) * mm, "end": v(-15, 108) * mm});
            skLineSegment(sketch, "E81", {"start": v(-15, 108) * mm, "end": v(-33, 90) * mm});
            skLineSegment(sketch, "E82.MirrorCS", {"start": v(15, 120) * mm, "end": v(15, 108) * mm});
            skLineSegment(sketch, "E83.MirrorCS", {"start": v(15, 108) * mm, "end": v(33, 90) * mm});
            skArc(sketch, "E84", {"start": v(15, 120) * mm, "mid": v(0, 135) * mm, "end": v(-15, 120) * mm});
            skCircle(sketch, "E85", {"center": v(0, 120) * mm, "radius": 6 * mm});
            skLineSegment(sketch, "E86", {"start": v(-80, 0) * mm, "end": v(80, 0) * mm, "construction": true});
            skLineSegment(sketch, "E87.MirrorCS", {"start": v(-15, -108) * mm, "end": v(-33, -90) * mm});
            skLineSegment(sketch, "E88.MirrorCS", {"start": v(-15, -120) * mm, "end": v(-15, -108) * mm});
            skArc(sketch, "E89.MirrorCS", {"start": v(15, -120) * mm, "mid": v(0, -135) * mm, "end": v(-15, -120) * mm});
            skLineSegment(sketch, "E90.MirrorCS", {"start": v(15, -120) * mm, "end": v(15, -108) * mm});
            skLineSegment(sketch, "E91.MirrorCS", {"start": v(15, -108) * mm, "end": v(33, -90) * mm});
            skCircle(sketch, "E92.MirrorC", {"center": v(0, -120) * mm, "radius": 6 * mm});
            skLineSegment(sketch, "E93.MirrorCS", {"start": v(0, -90) * mm, "end": v(0, -120) * mm, "construction": true});
            skSolve(sketch);
        }
        {
            var Q0;
            Q0=makeQuery(id+"F16.imprint","IMPRINT",FACE,{"disambiguationData":[TD([[makeQuery(id+"F16.imprint","IMPRINT",EDGE,{"derivedFrom":makeQuery(id+"F1.opExtrude","CAP_EDGE",EDGE,{"disambiguationData":[OSD([sQuery(id+"F0.wireOp",EDGE,"E1.left")])],"isStart":true})}),-1.0]])]});
            var Q1;
            Q1=makeQuery(id+"F16.imprint","IMPRINT",FACE,{"disambiguationData":[TD([[makeQuery(id+"F16.imprint","IMPRINT",EDGE,{"derivedFrom":sQuery(id+"F16.wireOp",EDGE,"E80")}),1.0]])]});
            var Q2;
            {var subQ0=sQuery(id+"F16.wireOp",EDGE,"E87.MirrorCS");Q2=makeQuery(id+"F16.imprint","IMPRINT",FACE,{"disambiguationData":[TD([[makeQuery(id+"F16.imprint","IMPRINT",EDGE,{"derivedFrom":subQ0}),-1.0]])]});}
            var Q3;
            Q3=makeQuery(id+"F2.opExtrude","CAP_FACE",FACE,{"disambiguationData":[OSD([sQuery(id+"F0.wireOp",EDGE,"E12"),sQuery(id+"F0.wireOp",EDGE,"E13"),sQuery(id+"F0.wireOp",EDGE,"E14"),sQuery(id+"F0.wireOp",EDGE,"E15"),sQuery(id+"F0.wireOp",EDGE,"E17.filletArc"),sQuery(id+"F0.wireOp",EDGE,"E18.filletArc"),sQuery(id+"F0.wireOp",EDGE,"E19.filletArc"),sQuery(id+"F0.wireOp",EDGE,"E20.filletArc"),sQuery(id+"F0.wireOp",EDGE,"E25.0"),sQuery(id+"F0.wireOp",EDGE,"E25.1"),sQuery(id+"F0.wireOp",EDGE,"E25.2"),sQuery(id+"F0.wireOp",EDGE,"E25.3"),sQuery(id+"F0.wireOp",EDGE,"E25.4"),sQuery(id+"F0.wireOp",EDGE,"E25.5"),sQuery(id+"F0.wireOp",EDGE,"E25.6"),sQuery(id+"F0.wireOp",EDGE,"E25.7")])],"isStart":false});
            extrude(context, id + "F17", {"entities" : qUnion([Q0, Q1, Q2]), "endBound" : BoundingType.UP_TO_SURFACE, "endBoundEntityFace" : qUnion([Q3]), "depth" : 25 * mm});
        }
    });
